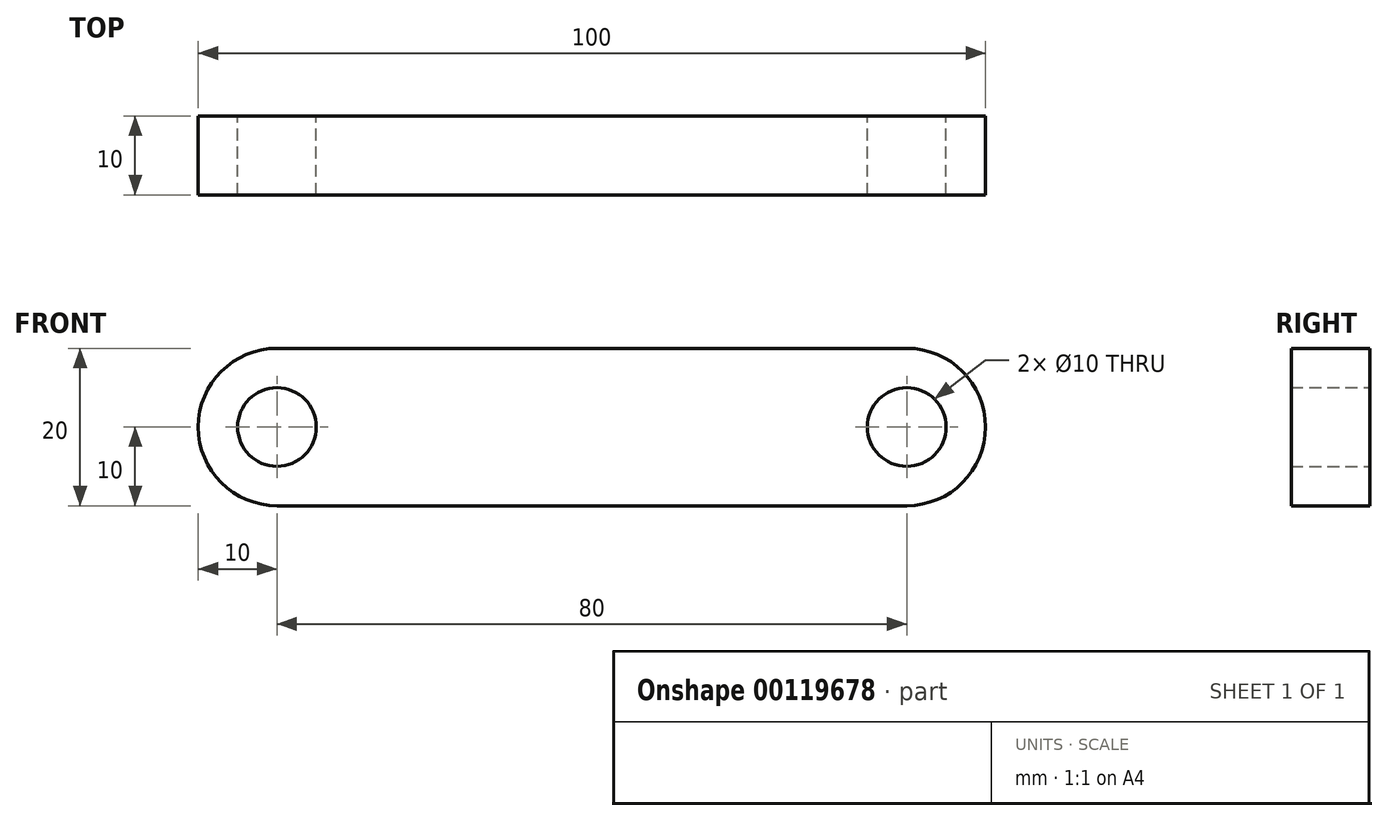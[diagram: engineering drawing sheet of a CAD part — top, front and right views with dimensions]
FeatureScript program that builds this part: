
annotation { "Feature Type Name" : "Feature", "Feature Type Description" : "" }
export const myFeature = defineFeature(function(context is Context, id is Id, definition is map)
    precondition{}
    {
        {
            var Q0;
            Q0=qCreatedBy(makeId("Front.planeOp"),FACE);
            var sketch = newSketch(context, id + "F0", { "sketchPlane" : qUnion([Q0])});
            skArc(sketch, "E0", {"start": v(0, 10) * mm, "mid": v(-10, 0) * mm, "end": v(0, -10) * mm});
            skLineSegment(sketch, "E1", {"start": v(0, 10) * mm, "end": v(80, 10) * mm});
            skLineSegment(sketch, "E2", {"start": v(0, -10) * mm, "end": v(80, -10) * mm});
            skArc(sketch, "E3", {"start": v(80, 10) * mm, "mid": v(90, 0) * mm, "end": v(80, -10) * mm});
            skCircle(sketch, "E4", {"center": v(0, 0) * mm, "radius": 5 * mm});
            skCircle(sketch, "E5", {"center": v(80, 0) * mm, "radius": 5 * mm});
            skSolve(sketch);
        }
        {
            var Q0;
            Q0 = qSketchRegion(id + "F0", true);
            extrude(context, id + "F1", {"entities" : qUnion([Q0]), "endBound" : BoundingType.SYMMETRIC, "depth" : 10 * mm});
        }
    });
